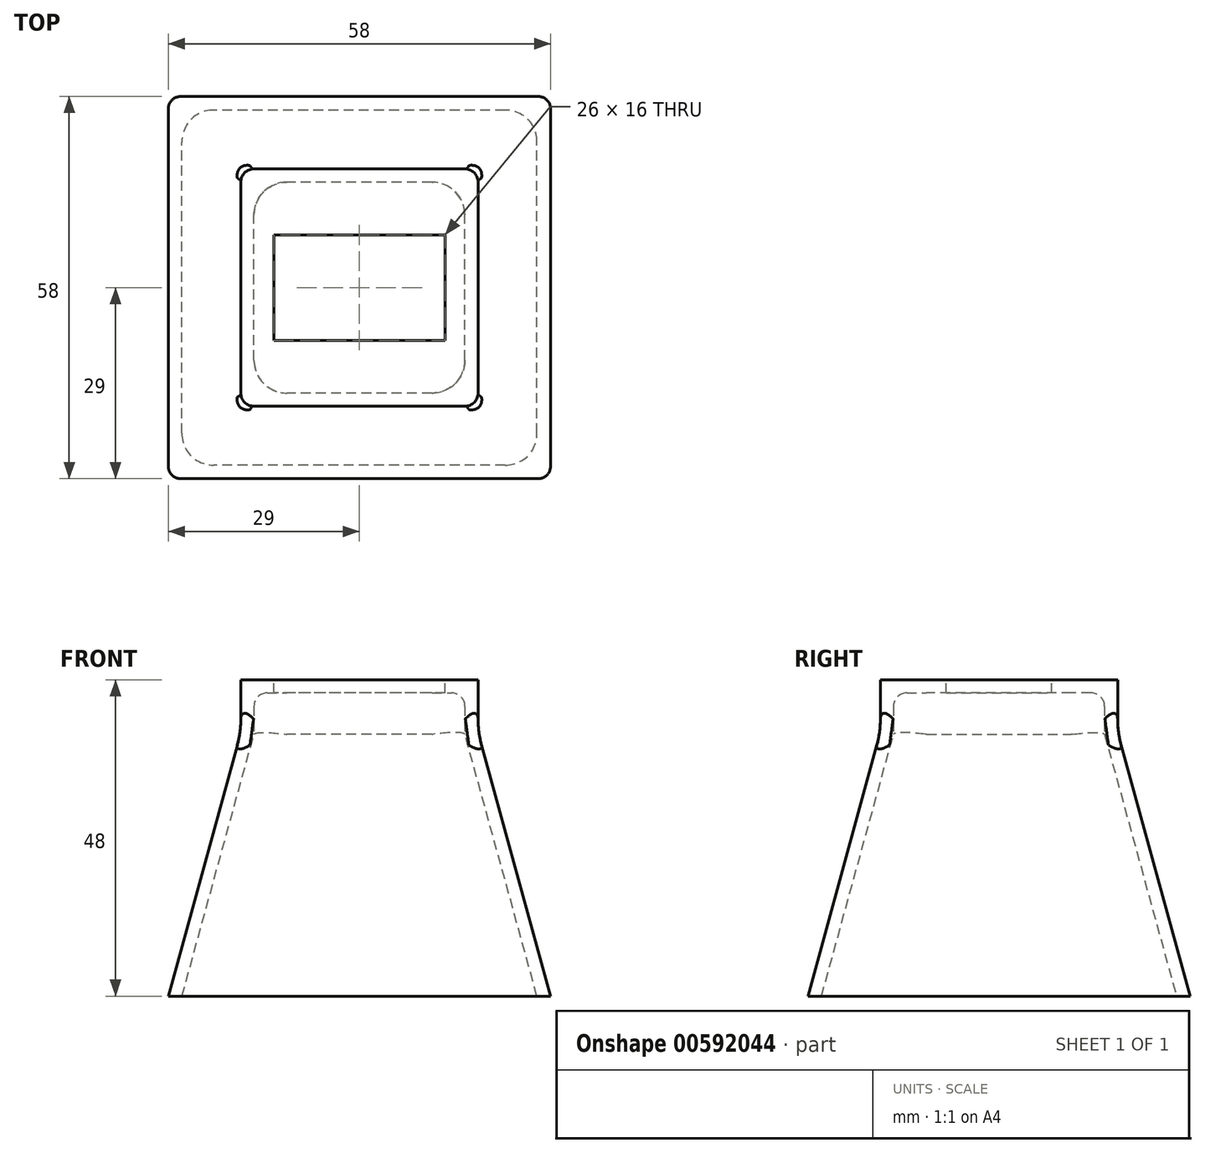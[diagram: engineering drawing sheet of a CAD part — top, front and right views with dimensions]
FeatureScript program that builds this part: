
annotation { "Feature Type Name" : "Feature", "Feature Type Description" : "" }
export const myFeature = defineFeature(function(context is Context, id is Id, definition is map)
    precondition{}
    {
        {
            var Q0;
            Q0=qCreatedBy(makeId("Top.planeOp"),FACE);
            var sketch = newSketch(context, id + "F0", { "sketchPlane" : qUnion([Q0])});
            skLineSegment(sketch, "E0.bottom", {"start": v(29, 29) * mm, "end": v(-29, 29) * mm});
            skLineSegment(sketch, "E0.top", {"start": v(29, -29) * mm, "end": v(-29, -29) * mm});
            skLineSegment(sketch, "E0.left", {"start": v(29, 29) * mm, "end": v(29, -29) * mm});
            skLineSegment(sketch, "E0.right", {"start": v(-29, 29) * mm, "end": v(-29, -29) * mm});
            skPoint(sketch, "E0.middle", {"position": v(0, 0) * mm});
            skSolve(sketch);
        }
        {
            var Q0;
            Q0=qCreatedBy(makeId("Top.planeOp"),FACE);
            cPlane(context, id + "F1", {"entities" : qUnion([Q0]), "cplaneType" : CPlaneType.OFFSET, "offset" : 40 * mm, "width" : 150 * mm, "height" : 150 * mm});
        }
        {
            var Q0;
            Q0=qCreatedBy(id+"F1.planeOp",FACE);
            var sketch = newSketch(context, id + "F2", { "sketchPlane" : qUnion([Q0])});
            skLineSegment(sketch, "E1.bottom", {"start": v(18, -18) * mm, "end": v(-18, -18) * mm});
            skLineSegment(sketch, "E1.top", {"start": v(18, 18) * mm, "end": v(-18, 18) * mm});
            skLineSegment(sketch, "E1.left", {"start": v(18, -18) * mm, "end": v(18, 18) * mm});
            skLineSegment(sketch, "E1.right", {"start": v(-18, -18) * mm, "end": v(-18, 18) * mm});
            skPoint(sketch, "E1.middle", {"position": v(0, 0) * mm});
            skSolve(sketch);
        }
        {
            var Q0;
            Q0=makeQuery(id+"F2.imprint","IMPRINT",FACE,{"disambiguationData":[TD([[makeQuery(id+"F2.imprint","IMPRINT",EDGE,{"derivedFrom":sQuery(id+"F2.wireOp",EDGE,"E1.bottom")}),-1.0]])]});
            var Q1;
            Q1=makeQuery(id+"F0.imprint","IMPRINT",FACE,{"disambiguationData":[TD([[makeQuery(id+"F0.imprint","IMPRINT",EDGE,{"derivedFrom":sQuery(id+"F0.wireOp",EDGE,"E0.bottom")}),1.0]])]});
            loft(context, id + "F3", {"sheetProfilesArray" : [{ "sheetProfileEntities" : qUnion([Q0]) }, { "sheetProfileEntities" : qUnion([Q1]) }]});
        }
        {
            var Q0;
            Q0=makeQuery(id+"F3.opLoft","CAP_FACE",FACE,{"disambiguationData":[OSD([makeQuery(id+"F2.imprint","IMPRINT",FACE,{"disambiguationData":[TD([[makeQuery(id+"F2.imprint","IMPRINT",EDGE,{"derivedFrom":sQuery(id+"F2.wireOp",EDGE,"E1.bottom")}),-1.0]])]})])],"isStart":true});
            extrude(context, id + "F4", {"entities" : qUnion([Q0]), "operationType" : NewBodyOperationType.ADD, "depth" : 8 * mm, "offsetDistance" : 25 * mm});
        }
        {
            var Q0;
            Q0=makeQuery(id+"F4.opExtrude","CAP_FACE",FACE,{"disambiguationData":[OSD([makeQuery(id+"F2.imprint","IMPRINT",FACE,{"disambiguationData":[TD([[makeQuery(id+"F2.imprint","IMPRINT",EDGE,{"derivedFrom":sQuery(id+"F2.wireOp",EDGE,"E1.bottom")}),-1.0]])]})])],"isStart":false});
            var sketch = newSketch(context, id + "F5", { "sketchPlane" : qUnion([Q0])});
            skLineSegment(sketch, "E2.bottom", {"start": v(13, -8) * mm, "end": v(-13, -8) * mm});
            skLineSegment(sketch, "E2.top", {"start": v(13, 8) * mm, "end": v(-13, 8) * mm});
            skLineSegment(sketch, "E2.left", {"start": v(13, -8) * mm, "end": v(13, 8) * mm});
            skLineSegment(sketch, "E2.right", {"start": v(-13, -8) * mm, "end": v(-13, 8) * mm});
            skPoint(sketch, "E2.middle", {"position": v(0, 0) * mm});
            skSolve(sketch);
        }
        {
            var Q0;
            Q0=makeQuery(id+"F3.opLoft","CAP_FACE",FACE,{"disambiguationData":[OSD([makeQuery(id+"F0.imprint","IMPRINT",FACE,{"disambiguationData":[TD([[makeQuery(id+"F0.imprint","IMPRINT",EDGE,{"derivedFrom":sQuery(id+"F0.wireOp",EDGE,"E0.bottom")}),1.0]])]})])],"isStart":true});
            shell(context, id + "F6", {"entities" : qUnion([Q0]), "thickness" : 2 * mm});
        }
        {
            var Q0;
            Q0=makeQuery(id+"F3.opLoft","SWEPT_EDGE",EDGE,{"disambiguationData":[OSD([sQuery(id+"F0.wireOp",EDGE,"E0.top"),sQuery(id+"F0.wireOp",EDGE,"E0.right"),sQuery(id+"F2.wireOp",EDGE,"E1.bottom"),sQuery(id+"F2.wireOp",EDGE,"E1.right")])]});
            var Q1;
            Q1=makeQuery(id+"F4.opExtrude","SWEPT_EDGE",EDGE,{"disambiguationData":[OSD([sQuery(id+"F2.wireOp",EDGE,"E1.bottom"),sQuery(id+"F2.wireOp",EDGE,"E1.right")])]});
            var Q2;
            Q2=makeQuery(id+"F3.opLoft","SWEPT_EDGE",EDGE,{"disambiguationData":[OSD([sQuery(id+"F0.wireOp",EDGE,"E0.top"),sQuery(id+"F0.wireOp",EDGE,"E0.left"),sQuery(id+"F2.wireOp",EDGE,"E1.bottom"),sQuery(id+"F2.wireOp",EDGE,"E1.left")])]});
            var Q3;
            Q3=makeQuery(id+"F4.opExtrude","SWEPT_EDGE",EDGE,{"disambiguationData":[OSD([sQuery(id+"F2.wireOp",EDGE,"E1.bottom"),sQuery(id+"F2.wireOp",EDGE,"E1.left")])]});
            var Q4;
            Q4=makeQuery(id+"F3.opLoft","SWEPT_EDGE",EDGE,{"disambiguationData":[OSD([sQuery(id+"F0.wireOp",EDGE,"E0.bottom"),sQuery(id+"F0.wireOp",EDGE,"E0.left"),sQuery(id+"F2.wireOp",EDGE,"E1.top"),sQuery(id+"F2.wireOp",EDGE,"E1.left")])]});
            var Q5;
            Q5=makeQuery(id+"F4.opExtrude","SWEPT_EDGE",EDGE,{"disambiguationData":[OSD([sQuery(id+"F2.wireOp",EDGE,"E1.top"),sQuery(id+"F2.wireOp",EDGE,"E1.left")])]});
            var Q6;
            Q6=makeQuery(id+"F3.opLoft","SWEPT_EDGE",EDGE,{"disambiguationData":[OSD([sQuery(id+"F0.wireOp",EDGE,"E0.bottom"),sQuery(id+"F0.wireOp",EDGE,"E0.right"),sQuery(id+"F2.wireOp",EDGE,"E1.top"),sQuery(id+"F2.wireOp",EDGE,"E1.right")])]});
            var Q7;
            Q7=makeQuery(id+"F4.opExtrude","SWEPT_EDGE",EDGE,{"disambiguationData":[OSD([sQuery(id+"F2.wireOp",EDGE,"E1.top"),sQuery(id+"F2.wireOp",EDGE,"E1.right")])]});
            fillet(context, id + "F7", {"entities" : qUnion([Q0, Q1, Q2, Q3, Q4, Q5, Q6, Q7]), "radius" : 2 * mm, "tangentPropagation" : true, "allowEdgeOverflow" : false});
        }
        {
            var Q0;
            {var subQ0=sQuery(id+"F2.wireOp",EDGE,"E1.right");var subQ1=sQuery(id+"F2.wireOp",EDGE,"E1.left");var subQ2=sQuery(id+"F2.wireOp",EDGE,"E1.top");Q0=makeQuery(id+"F4.boolean.opBoolean","MERGE",EDGE,{"derivedFrom":[makeQuery(id+"F3.opLoft","MID_CAP_EDGE",EDGE,{"disambiguationData":[OSD([subQ2,subQ1,subQ0])],"capPos":0.0}),makeQuery(id+"F4.opExtrude","CAP_EDGE",EDGE,{"disambiguationData":[OSD([subQ2,subQ1,subQ0])],"isStart":true})]});}
            fillet(context, id + "F8", {"entities" : qUnion([Q0]), "radius" : 15 * mm, "tangentPropagation" : true, "allowEdgeOverflow" : false});
        }
        {
            var Q0;
            Q0=makeQuery(id+"F5.imprint","IMPRINT",FACE,{"disambiguationData":[TD([[makeQuery(id+"F5.imprint","IMPRINT",EDGE,{"derivedFrom":sQuery(id+"F5.wireOp",EDGE,"E2.bottom")}),-1.0]])]});
            extrude(context, id + "F9", {"entities" : qUnion([Q0]), "operationType" : NewBodyOperationType.REMOVE, "oppositeDirection" : true, "depth" : 25 * mm, "offsetDistance" : 25 * mm});
        }
        {
            var Q0;
            Q0=makeQuery(id+"F6.opShell","OFFSET_EDGE",EDGE,{"disambiguationData":[OSD([sQuery(id+"F0.wireOp",EDGE,"E0.top"),sQuery(id+"F0.wireOp",EDGE,"E0.right"),sQuery(id+"F2.wireOp",EDGE,"E1.bottom"),sQuery(id+"F2.wireOp",EDGE,"E1.right")])]});
            var Q1;
            Q1=makeQuery(id+"F6.opShell","OFFSET_EDGE",EDGE,{"disambiguationData":[OSD([sQuery(id+"F0.wireOp",EDGE,"E0.top"),sQuery(id+"F0.wireOp",EDGE,"E0.left"),sQuery(id+"F2.wireOp",EDGE,"E1.bottom"),sQuery(id+"F2.wireOp",EDGE,"E1.left")])]});
            var Q2;
            Q2=makeQuery(id+"F6.opShell","OFFSET_EDGE",EDGE,{"disambiguationData":[OSD([sQuery(id+"F0.wireOp",EDGE,"E0.bottom"),sQuery(id+"F0.wireOp",EDGE,"E0.left"),sQuery(id+"F2.wireOp",EDGE,"E1.top"),sQuery(id+"F2.wireOp",EDGE,"E1.left")])]});
            var Q3;
            Q3=makeQuery(id+"F6.opShell","OFFSET_EDGE",EDGE,{"disambiguationData":[OSD([sQuery(id+"F0.wireOp",EDGE,"E0.bottom"),sQuery(id+"F0.wireOp",EDGE,"E0.right"),sQuery(id+"F2.wireOp",EDGE,"E1.top"),sQuery(id+"F2.wireOp",EDGE,"E1.right")])]});
            var Q4;
            Q4=makeQuery(id+"F6.opShell","OFFSET_EDGE",EDGE,{"disambiguationData":[OSD([sQuery(id+"F2.wireOp",EDGE,"E1.top"),sQuery(id+"F2.wireOp",EDGE,"E1.right")])]});
            var Q5;
            Q5=makeQuery(id+"F6.opShell","OFFSET_EDGE",EDGE,{"disambiguationData":[OSD([sQuery(id+"F2.wireOp",EDGE,"E1.top"),sQuery(id+"F2.wireOp",EDGE,"E1.left")])]});
            var Q6;
            Q6=makeQuery(id+"F6.opShell","OFFSET_EDGE",EDGE,{"disambiguationData":[OSD([sQuery(id+"F2.wireOp",EDGE,"E1.bottom"),sQuery(id+"F2.wireOp",EDGE,"E1.left")])]});
            var Q7;
            Q7=makeQuery(id+"F6.opShell","OFFSET_EDGE",EDGE,{"disambiguationData":[OSD([sQuery(id+"F2.wireOp",EDGE,"E1.bottom"),sQuery(id+"F2.wireOp",EDGE,"E1.right")])]});
            fillet(context, id + "F10", {"entities" : qUnion([Q0, Q1, Q2, Q3, Q4, Q5, Q6, Q7]), "radius" : 5 * mm, "tangentPropagation" : true, "allowEdgeOverflow" : false});
        }
        {
            var Q0;
            {var subQ0=sQuery(id+"F2.wireOp",EDGE,"E1.right");var subQ1=sQuery(id+"F2.wireOp",EDGE,"E1.left");var subQ2=sQuery(id+"F2.wireOp",EDGE,"E1.bottom");Q0=makeQuery(id+"F6.opShell","OFFSET_EDGE",EDGE,{"disambiguationData":[OSD([subQ2,subQ1,subQ0]),TDD([makeQuery(id+"F4.opExtrude","CAP_EDGE",EDGE,{"disambiguationData":[OSD([subQ2,subQ1,subQ0])],"isStart":false})])]});}
            fillet(context, id + "F11", {"entities" : qUnion([Q0]), "radius" : 2 * mm, "tangentPropagation" : true, "allowEdgeOverflow" : false});
        }
    });
